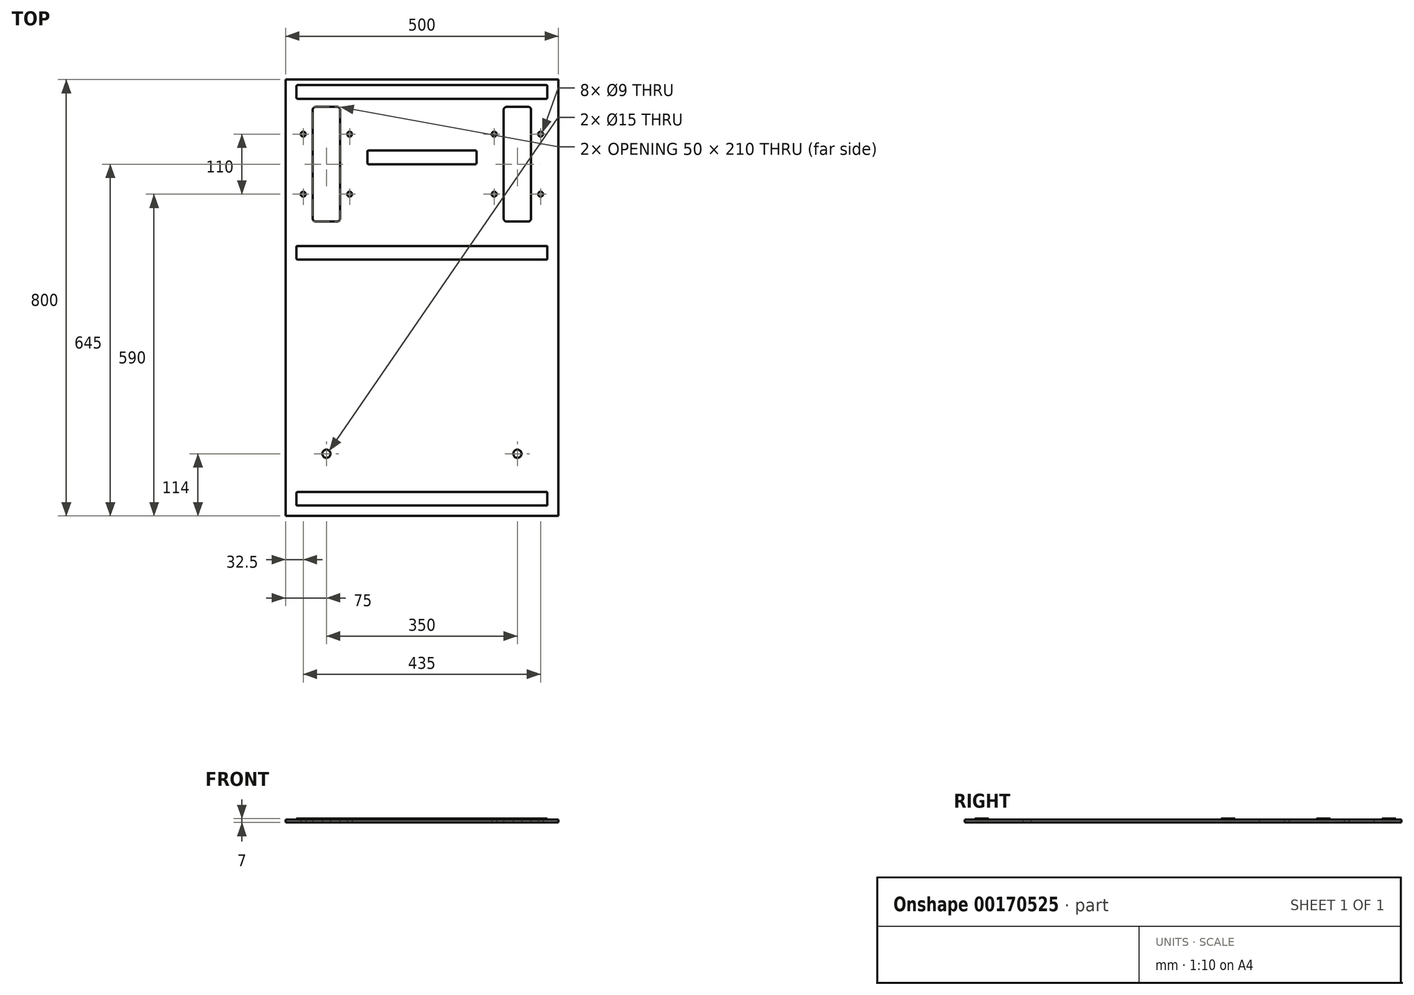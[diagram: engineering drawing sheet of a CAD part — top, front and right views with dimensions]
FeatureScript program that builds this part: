
annotation { "Feature Type Name" : "Feature", "Feature Type Description" : "" }
export const myFeature = defineFeature(function(context is Context, id is Id, definition is map)
    precondition{}
    {
        {
            var Q0;
            Q0=qCreatedBy(makeId("Top.planeOp"),FACE);
            var sketch = newSketch(context, id + "F0", { "sketchPlane" : qUnion([Q0])});
            skLineSegment(sketch, "E0.bottom", {"start": v(-250, 225) * mm, "end": v(250, 225) * mm});
            skLineSegment(sketch, "E0.top", {"start": v(-250, -575) * mm, "end": v(250, -575) * mm});
            skLineSegment(sketch, "E0.left", {"start": v(-250, 225) * mm, "end": v(-250, -575) * mm});
            skLineSegment(sketch, "E0.right", {"start": v(250, 225) * mm, "end": v(250, -575) * mm});
            skLineSegment(sketch, "E1", {"start": v(0, 225) * mm, "end": v(0, -281.03) * mm, "construction": true});
            skLineSegment(sketch, "E2", {"start": v(250, 0) * mm, "end": v(-550, 0) * mm, "construction": true});
            skLineSegment(sketch, "E3.bottom", {"start": v(-195, 175) * mm, "end": v(-155, 175) * mm});
            skLineSegment(sketch, "E3.top", {"start": v(-195, -35) * mm, "end": v(-155, -35) * mm});
            skLineSegment(sketch, "E3.left", {"start": v(-200, 170) * mm, "end": v(-200, -30) * mm});
            skLineSegment(sketch, "E3.right", {"start": v(-150, 170) * mm, "end": v(-150, -30) * mm});
            skCircle(sketch, "E4", {"center": v(-217.5, 125) * mm, "radius": 4.5 * mm});
            skLineSegment(sketch, "E5", {"start": v(-200, 70) * mm, "end": v(-239.44, 70) * mm, "construction": true});
            skLineSegment(sketch, "E6", {"start": v(-175, 175) * mm, "end": v(-175, -66.2) * mm, "construction": true});
            skCircle(sketch, "E7.MirrorC", {"center": v(-217.5, 15) * mm, "radius": 4.5 * mm});
            skCircle(sketch, "E8.MirrorC", {"center": v(-132.5, 125) * mm, "radius": 4.5 * mm});
            skCircle(sketch, "E9.MirrorC", {"center": v(-132.5, 15) * mm, "radius": 4.5 * mm});
            skPoint(sketch, "E10.visualSharp", {"position": v(-200, 175) * mm});
            skArc(sketch, "E10.filletArc", {"start": v(-195, 175) * mm, "mid": v(-198.54, 173.54) * mm, "end": v(-200, 170) * mm});
            skPoint(sketch, "E11.visualSharp", {"position": v(-150, 175) * mm});
            skArc(sketch, "E11.filletArc", {"start": v(-150, 170) * mm, "mid": v(-151.46, 173.54) * mm, "end": v(-155, 175) * mm});
            skPoint(sketch, "E12.visualSharp", {"position": v(-200, -35) * mm});
            skArc(sketch, "E12.filletArc", {"start": v(-200, -30) * mm, "mid": v(-198.54, -33.54) * mm, "end": v(-195, -35) * mm});
            skPoint(sketch, "E13.visualSharp", {"position": v(-150, -35) * mm});
            skArc(sketch, "E13.filletArc", {"start": v(-155, -35) * mm, "mid": v(-151.46, -33.54) * mm, "end": v(-150, -30) * mm});
            skArc(sketch, "E14.MirrorCS", {"start": v(155, -35) * mm, "mid": v(151.46, -33.54) * mm, "end": v(150, -30) * mm});
            skArc(sketch, "E15.MirrorCS", {"start": v(150, 170) * mm, "mid": v(151.46, 173.54) * mm, "end": v(155, 175) * mm});
            skArc(sketch, "E16.MirrorCS", {"start": v(200, -30) * mm, "mid": v(198.54, -33.54) * mm, "end": v(195, -35) * mm});
            skArc(sketch, "E17.MirrorCS", {"start": v(195, 175) * mm, "mid": v(198.54, 173.54) * mm, "end": v(200, 170) * mm});
            skCircle(sketch, "E18.MirrorC", {"center": v(217.5, 15) * mm, "radius": 4.5 * mm});
            skCircle(sketch, "E19.MirrorC", {"center": v(132.5, 125) * mm, "radius": 4.5 * mm});
            skCircle(sketch, "E20.MirrorC", {"center": v(132.5, 15) * mm, "radius": 4.5 * mm});
            skCircle(sketch, "E21.MirrorC", {"center": v(217.5, 125) * mm, "radius": 4.5 * mm});
            skPoint(sketch, "E22.MirrorP", {"position": v(200, -35) * mm});
            skLineSegment(sketch, "E23.MirrorCS", {"start": v(195, 175) * mm, "end": v(155, 175) * mm});
            skLineSegment(sketch, "E24.MirrorCS", {"start": v(195, -35) * mm, "end": v(155, -35) * mm});
            skPoint(sketch, "E25.MirrorP", {"position": v(150, -35) * mm});
            skPoint(sketch, "E26.MirrorP", {"position": v(150, 175) * mm});
            skLineSegment(sketch, "E27.MirrorCS", {"start": v(200, 170) * mm, "end": v(200, -30) * mm});
            skLineSegment(sketch, "E28.MirrorCS", {"start": v(150, 170) * mm, "end": v(150, -30) * mm});
            skPoint(sketch, "E29.MirrorP", {"position": v(200, 175) * mm});
            skLineSegment(sketch, "E30", {"start": v(-175, -428.1) * mm, "end": v(-175, -642.63) * mm, "construction": true});
            skCircle(sketch, "E31", {"center": v(-175, -461) * mm, "radius": 7.5 * mm});
            skCircle(sketch, "E32.MirrorC", {"center": v(175, -461) * mm, "radius": 7.5 * mm});
            skSolve(sketch);
        }
        {
            var Q0;
            Q0=makeQuery(id+"F0.imprint","IMPRINT",FACE,{"disambiguationData":[TD([[makeQuery(id+"F0.imprint","IMPRINT",EDGE,{"derivedFrom":sQuery(id+"F0.wireOp",EDGE,"E0.bottom")}),-1.0]])]});
            extrude(context, id + "F1", {"entities" : qUnion([Q0]), "depth" : 5 * mm});
        }
        {
            var Q0;
            Q0=makeQuery(id+"F1.opExtrude","CAP_FACE",FACE,{"disambiguationData":[OSD([sQuery(id+"F0.wireOp",EDGE,"E0.bottom"),sQuery(id+"F0.wireOp",EDGE,"E0.top"),sQuery(id+"F0.wireOp",EDGE,"E0.left"),sQuery(id+"F0.wireOp",EDGE,"E0.right"),sQuery(id+"F0.wireOp",EDGE,"E3.bottom"),sQuery(id+"F0.wireOp",EDGE,"E3.top"),sQuery(id+"F0.wireOp",EDGE,"E3.left"),sQuery(id+"F0.wireOp",EDGE,"E3.right"),sQuery(id+"F0.wireOp",EDGE,"E4"),sQuery(id+"F0.wireOp",EDGE,"E7.MirrorC"),sQuery(id+"F0.wireOp",EDGE,"E8.MirrorC"),sQuery(id+"F0.wireOp",EDGE,"E9.MirrorC"),sQuery(id+"F0.wireOp",EDGE,"E10.filletArc"),sQuery(id+"F0.wireOp",EDGE,"E11.filletArc"),sQuery(id+"F0.wireOp",EDGE,"E12.filletArc"),sQuery(id+"F0.wireOp",EDGE,"E13.filletArc"),sQuery(id+"F0.wireOp",EDGE,"E14.MirrorCS"),sQuery(id+"F0.wireOp",EDGE,"E15.MirrorCS"),sQuery(id+"F0.wireOp",EDGE,"E16.MirrorCS"),sQuery(id+"F0.wireOp",EDGE,"E17.MirrorCS"),sQuery(id+"F0.wireOp",EDGE,"E18.MirrorC"),sQuery(id+"F0.wireOp",EDGE,"E19.MirrorC"),sQuery(id+"F0.wireOp",EDGE,"E20.MirrorC"),sQuery(id+"F0.wireOp",EDGE,"E21.MirrorC"),sQuery(id+"F0.wireOp",EDGE,"E23.MirrorCS"),sQuery(id+"F0.wireOp",EDGE,"E24.MirrorCS"),sQuery(id+"F0.wireOp",EDGE,"E27.MirrorCS"),sQuery(id+"F0.wireOp",EDGE,"E28.MirrorCS"),sQuery(id+"F0.wireOp",EDGE,"E31"),sQuery(id+"F0.wireOp",EDGE,"E32.MirrorC")])],"isStart":false});
            var sketch = newSketch(context, id + "F2", { "sketchPlane" : qUnion([Q0])});
            skLineSegment(sketch, "E33.bottom", {"start": v(-228, 215) * mm, "end": v(228, 215) * mm});
            skLineSegment(sketch, "E33.top", {"start": v(-228, 190) * mm, "end": v(228, 190) * mm});
            skLineSegment(sketch, "E33.left", {"start": v(-230, 213) * mm, "end": v(-230, 192) * mm});
            skLineSegment(sketch, "E33.right", {"start": v(230, 213) * mm, "end": v(230, 192) * mm});
            skLineSegment(sketch, "E34", {"start": v(0, 225) * mm, "end": v(0, 110.2) * mm, "construction": true});
            skPoint(sketch, "E35.visualSharp", {"position": v(-230, 215) * mm});
            skArc(sketch, "E35.filletArc", {"start": v(-228, 215) * mm, "mid": v(-229.41, 214.41) * mm, "end": v(-230, 213) * mm});
            skPoint(sketch, "E36.visualSharp", {"position": v(-230, 190) * mm});
            skArc(sketch, "E36.filletArc", {"start": v(-230, 192) * mm, "mid": v(-229.41, 190.59) * mm, "end": v(-228, 190) * mm});
            skPoint(sketch, "E37.visualSharp", {"position": v(230, 215) * mm});
            skArc(sketch, "E37.filletArc", {"start": v(230, 213) * mm, "mid": v(229.41, 214.41) * mm, "end": v(228, 215) * mm});
            skPoint(sketch, "E38.visualSharp", {"position": v(230, 190) * mm});
            skArc(sketch, "E38.filletArc", {"start": v(228, 190) * mm, "mid": v(229.41, 190.59) * mm, "end": v(230, 192) * mm});
            skLineSegment(sketch, "E39.bottom", {"start": v(-98, 95) * mm, "end": v(98, 95) * mm});
            skLineSegment(sketch, "E39.top", {"start": v(-98, 70) * mm, "end": v(98, 70) * mm});
            skLineSegment(sketch, "E39.left", {"start": v(-100, 93) * mm, "end": v(-100, 72) * mm});
            skLineSegment(sketch, "E39.right", {"start": v(100, 93) * mm, "end": v(100, 72) * mm});
            skPoint(sketch, "E40.visualSharp", {"position": v(-100, 95) * mm});
            skArc(sketch, "E40.filletArc", {"start": v(-98, 95) * mm, "mid": v(-99.41, 94.41) * mm, "end": v(-100, 93) * mm});
            skPoint(sketch, "E41.visualSharp", {"position": v(-100, 70) * mm});
            skArc(sketch, "E41.filletArc", {"start": v(-100, 72) * mm, "mid": v(-99.41, 70.59) * mm, "end": v(-98, 70) * mm});
            skPoint(sketch, "E42.visualSharp", {"position": v(100, 95) * mm});
            skArc(sketch, "E42.filletArc", {"start": v(100, 93) * mm, "mid": v(99.41, 94.41) * mm, "end": v(98, 95) * mm});
            skPoint(sketch, "E43.visualSharp", {"position": v(100, 70) * mm});
            skArc(sketch, "E43.filletArc", {"start": v(98, 70) * mm, "mid": v(99.41, 70.59) * mm, "end": v(100, 72) * mm});
            skLineSegment(sketch, "E44.bottom", {"start": v(-228, -79.87) * mm, "end": v(228, -79.87) * mm});
            skLineSegment(sketch, "E44.top", {"start": v(-228, -104.87) * mm, "end": v(228, -104.87) * mm});
            skLineSegment(sketch, "E44.left", {"start": v(-230, -81.87) * mm, "end": v(-230, -102.87) * mm});
            skLineSegment(sketch, "E44.right", {"start": v(230, -81.87) * mm, "end": v(230, -102.87) * mm});
            skPoint(sketch, "E45.visualSharp", {"position": v(-230, -79.87) * mm});
            skArc(sketch, "E45.filletArc", {"start": v(-228, -79.87) * mm, "mid": v(-229.41, -80.46) * mm, "end": v(-230, -81.87) * mm});
            skPoint(sketch, "E46.visualSharp", {"position": v(-230, -104.87) * mm});
            skArc(sketch, "E46.filletArc", {"start": v(-230, -102.87) * mm, "mid": v(-229.41, -104.29) * mm, "end": v(-228, -104.87) * mm});
            skPoint(sketch, "E47.visualSharp", {"position": v(230, -79.87) * mm});
            skArc(sketch, "E47.filletArc", {"start": v(230, -81.87) * mm, "mid": v(229.41, -80.46) * mm, "end": v(228, -79.87) * mm});
            skPoint(sketch, "E48.visualSharp", {"position": v(230, -104.87) * mm});
            skArc(sketch, "E48.filletArc", {"start": v(228, -104.87) * mm, "mid": v(229.41, -104.29) * mm, "end": v(230, -102.87) * mm});
            skLineSegment(sketch, "E49.bottom", {"start": v(-228, -531.05) * mm, "end": v(228, -531.05) * mm});
            skLineSegment(sketch, "E49.top", {"start": v(-228, -556.05) * mm, "end": v(228, -556.05) * mm});
            skLineSegment(sketch, "E49.left", {"start": v(-230, -533.05) * mm, "end": v(-230, -554.05) * mm});
            skLineSegment(sketch, "E49.right", {"start": v(230, -533.05) * mm, "end": v(230, -554.05) * mm});
            skPoint(sketch, "E50.visualSharp", {"position": v(-230, -531.05) * mm});
            skArc(sketch, "E50.filletArc", {"start": v(-228, -531.05) * mm, "mid": v(-229.41, -531.63) * mm, "end": v(-230, -533.05) * mm});
            skPoint(sketch, "E51.visualSharp", {"position": v(-230, -556.05) * mm});
            skArc(sketch, "E51.filletArc", {"start": v(-230, -554.05) * mm, "mid": v(-229.41, -555.46) * mm, "end": v(-228, -556.05) * mm});
            skPoint(sketch, "E52.visualSharp", {"position": v(230, -531.05) * mm});
            skArc(sketch, "E52.filletArc", {"start": v(230, -533.05) * mm, "mid": v(229.41, -531.63) * mm, "end": v(228, -531.05) * mm});
            skPoint(sketch, "E53.visualSharp", {"position": v(230, -556.05) * mm});
            skArc(sketch, "E53.filletArc", {"start": v(228, -556.05) * mm, "mid": v(229.41, -555.46) * mm, "end": v(230, -554.05) * mm});
            skSolve(sketch);
        }
        {
            var Q0;
            Q0=makeQuery(id+"F2.imprint","IMPRINT",FACE,{"disambiguationData":[TD([[makeQuery(id+"F2.imprint","IMPRINT",EDGE,{"derivedFrom":sQuery(id+"F2.wireOp",EDGE,"E33.bottom")}),-1.0]])]});
            var Q1;
            Q1=makeQuery(id+"F2.imprint","IMPRINT",FACE,{"disambiguationData":[TD([[makeQuery(id+"F2.imprint","IMPRINT",EDGE,{"derivedFrom":sQuery(id+"F2.wireOp",EDGE,"E39.bottom")}),-1.0]])]});
            var Q2;
            Q2=makeQuery(id+"F2.imprint","IMPRINT",FACE,{"disambiguationData":[TD([[makeQuery(id+"F2.imprint","IMPRINT",EDGE,{"derivedFrom":sQuery(id+"F2.wireOp",EDGE,"E44.bottom")}),-1.0]])]});
            var Q3;
            Q3=makeQuery(id+"F2.imprint","IMPRINT",FACE,{"disambiguationData":[TD([[makeQuery(id+"F2.imprint","IMPRINT",EDGE,{"derivedFrom":sQuery(id+"F2.wireOp",EDGE,"E49.bottom")}),-1.0]])]});
            extrude(context, id + "F3", {"entities" : qUnion([Q0, Q1, Q2, Q3]), "operationType" : NewBodyOperationType.ADD, "depth" : 2 * mm});
        }
    });
